# Revit family: Paraplegic Box CC Pan Cistern Mech no seat
name_source: partatom
category: Plumbing Fixtures
units: mm (PartAtom-declared; Revit-internal decimal feet)

## family parameters
Always vertical = Yes
Cut with Voids When Loaded = No
Enable Cutting in Views = No
Host = Wall
Maintain Annotation Orientation = No
OmniClass Number = 23.45.00.00
OmniClass Title = Sanitary, Laundry, and Cleaning Equipment
Part Type = Normal
Room Calculation Point = No
Round Connector Dimension = Use Diameter
Shared = No

## types (2) — shared parameters
Category = Paraplegic / Medical
Ceramic = Ceramic
Colour = White
Grab Rail = Silver
Manufacturer = Lecico SA
Material = Vitreous China
Silver = Silver
Technical Dimensions = W443 x H855 x D731mm
URL = https://www.lecicosa.co.za
zero-valued in all types: Default Elevation

## per-type parameters (varying)
| type | Grab Rails | Product Code |
| Paraplegic Box CC Pan Cistern Mech no seat | No | PARSETCCB0NOSBE |
| Paraplegic Box CC Pan Cistern Mech Rails no seat | Yes | PARSETCCB0RAIBE |

note: column(s) folded — value = type name in every type: Model

## geometry (parser evidence)
native form markers: Blend x4, Sweep x5
no freeform markers — native parametric forms only
